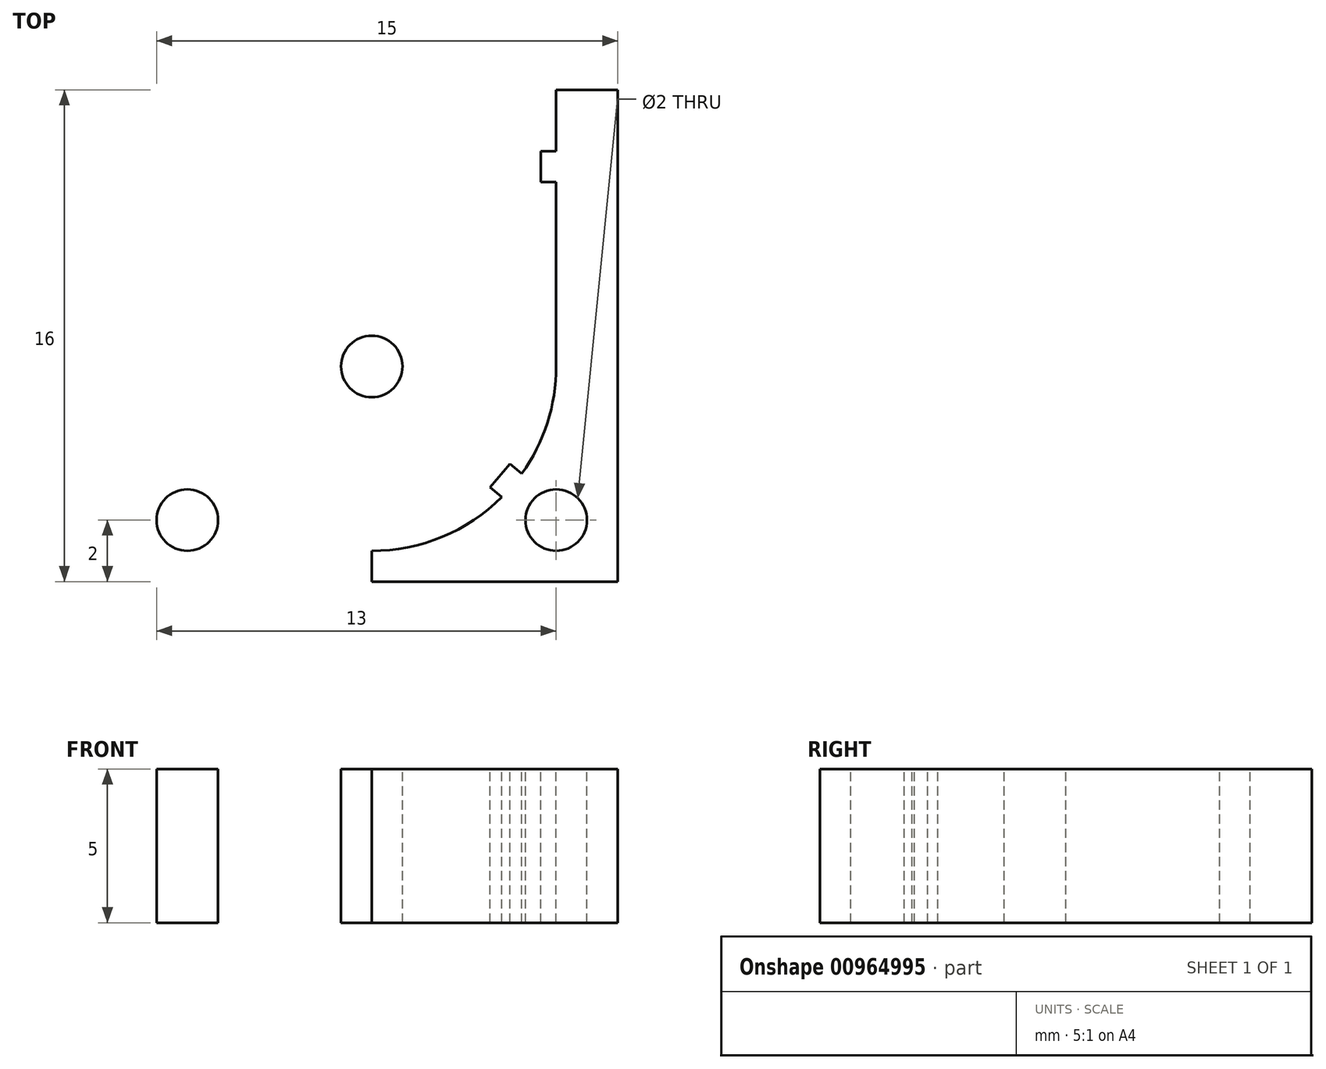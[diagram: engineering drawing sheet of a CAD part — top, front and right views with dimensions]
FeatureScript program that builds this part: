
annotation { "Feature Type Name" : "Feature", "Feature Type Description" : "" }
export const myFeature = defineFeature(function(context is Context, id is Id, definition is map)
    precondition{}
    {
        {
            var Q0;
            Q0=qCreatedBy(makeId("Top.planeOp"),FACE);
            var sketch = newSketch(context, id + "F0", { "sketchPlane" : qUnion([Q0])});
            skLineSegment(sketch, "E0.bottom", {"start": v(0, 0) * mm, "end": v(-16, 0) * mm});
            skLineSegment(sketch, "E0.top", {"start": v(0, 16) * mm, "end": v(-16, 16) * mm});
            skLineSegment(sketch, "E0.left", {"start": v(0, 0) * mm, "end": v(0, 16) * mm});
            skLineSegment(sketch, "E0.right", {"start": v(-16, 0) * mm, "end": v(-16, 16) * mm});
            skSolve(sketch);
        }
        {
            var Q0;
            Q0=makeQuery(id+"F0.imprint","IMPRINT",FACE,{"disambiguationData":[TD([[makeQuery(id+"F0.imprint","IMPRINT",EDGE,{"derivedFrom":sQuery(id+"F0.wireOp",EDGE,"E0.bottom")}),-1.0]])]});
            extrude(context, id + "F1", {"entities" : qUnion([Q0]), "depth" : 5 * mm, "offsetDistance" : 25 * mm});
        }
        {
            var Q0;
            Q0=makeQuery(id+"F1.opExtrude","CAP_FACE",FACE,{"disambiguationData":[OSD([sQuery(id+"F0.wireOp",EDGE,"E0.bottom"),sQuery(id+"F0.wireOp",EDGE,"E0.top"),sQuery(id+"F0.wireOp",EDGE,"E0.left"),sQuery(id+"F0.wireOp",EDGE,"E0.right")])],"isStart":false});
            var sketch = newSketch(context, id + "F2", { "sketchPlane" : qUnion([Q0])});
            skLineSegment(sketch, "E1", {"start": v(-16, 16) * mm, "end": v(-14, 16) * mm});
            skLineSegment(sketch, "E2", {"start": v(-14, 16) * mm, "end": v(-2, 16) * mm});
            skLineSegment(sketch, "E3", {"start": v(-2, 16) * mm, "end": v(0, 16) * mm});
            skLineSegment(sketch, "E4.bottom", {"start": v(-14, 16) * mm, "end": v(-12, 16) * mm});
            skLineSegment(sketch, "E4.top", {"start": v(-14, 7) * mm, "end": v(-12, 7) * mm});
            skLineSegment(sketch, "E4.left", {"start": v(-14, 16) * mm, "end": v(-14, 7) * mm});
            skLineSegment(sketch, "E4.right", {"start": v(-12, 16) * mm, "end": v(-12, 7) * mm});
            skLineSegment(sketch, "E5.bottom", {"start": v(-2, 16) * mm, "end": v(-4, 16) * mm});
            skLineSegment(sketch, "E5.top", {"start": v(-2, 7) * mm, "end": v(-4, 7) * mm});
            skLineSegment(sketch, "E5.left", {"start": v(-2, 16) * mm, "end": v(-2, 7) * mm});
            skLineSegment(sketch, "E5.right", {"start": v(-4, 16) * mm, "end": v(-4, 7) * mm});
            skArc(sketch, "E6", {"start": v(-12, 7) * mm, "mid": v(-8, 3) * mm, "end": v(-4, 7) * mm});
            skArc(sketch, "E7", {"start": v(-14, 7) * mm, "mid": v(-8, 1) * mm, "end": v(-2, 7) * mm});
            skLineSegment(sketch, "E8.0", {"start": v(-6, 16) * mm, "end": v(-6, 7) * mm});
            skArc(sketch, "E8.1", {"start": v(-10, 7) * mm, "mid": v(-8, 5) * mm, "end": v(-6, 7) * mm});
            skLineSegment(sketch, "E8.2", {"start": v(-10, 16) * mm, "end": v(-10, 7) * mm});
            skLineSegment(sketch, "E9", {"start": v(-8, 16) * mm, "end": v(-8, 7) * mm});
            skSolve(sketch);
        }
        {
            var Q0;
            Q0=makeQuery(id+"F2.imprint","IMPRINT",FACE,{"disambiguationData":[TD([[makeQuery(id+"F2.imprint","IMPRINT",EDGE,{"derivedFrom":sQuery(id+"F2.wireOp",EDGE,"E4.top")}),1.0]])]});
            var Q1;
            Q1=makeQuery(id+"F2.imprint","IMPRINT",FACE,{"disambiguationData":[TD([[makeQuery(id+"F2.imprint","IMPRINT",EDGE,{"derivedFrom":sQuery(id+"F2.wireOp",EDGE,"E4.top")}),-1.0]])]});
            var Q2;
            {var subQ3=sQuery(id+"F2.wireOp",EDGE,"E4.right");Q2=makeQuery(id+"F2.imprint","IMPRINT",FACE,{"disambiguationData":[TD([[makeQuery(id+"F2.imprint","IMPRINT",EDGE,{"derivedFrom":subQ3}),1.0]])]});}
            var Q3;
            Q3=makeQuery(id+"F2.imprint","IMPRINT",FACE,{"disambiguationData":[TD([[makeQuery(id+"F2.imprint","IMPRINT",EDGE,{"derivedFrom":sQuery(id+"F2.wireOp",EDGE,"E5.top")}),-1.0]])]});
            var Q4;
            Q4=makeQuery(id+"F2.imprint","IMPRINT",FACE,{"disambiguationData":[TD([[makeQuery(id+"F2.imprint","IMPRINT",EDGE,{"derivedFrom":sQuery(id+"F2.wireOp",EDGE,"E4.top")}),1.0]])]});
            var Q5;
            {var subQ4=sQuery(id+"F2.wireOp",EDGE,"v4n3mYmn-XXXl-4wGk-IPKp-ZQGeS8t006bx.top");Q5=makeQuery(id+"F2.imprint","IMPRINT",FACE,{"disambiguationData":[TD([[makeQuery(id+"F2.imprint","IMPRINT",EDGE,{"derivedFrom":subQ4}),-1.0]])]});}
            extrude(context, id + "F3", {"entities" : qUnion([Q0, Q1, Q2, Q3, Q4, Q5]), "operationType" : NewBodyOperationType.REMOVE, "oppositeDirection" : true, "depth" : 1.5 * mm, "offsetDistance" : 25 * mm});
        }
        {
            var Q0;
            Q0=makeQuery(id+"F3.boolean.opBoolean","COPY",FACE,{"derivedFrom":makeQuery(id+"F3.opExtrude","CAP_FACE",FACE,{"disambiguationData":[OSD([sQuery(id+"F2.wireOp",EDGE,"E2"),sQuery(id+"F2.wireOp",EDGE,"E4.left"),sQuery(id+"F2.wireOp",EDGE,"E5.left"),sQuery(id+"F2.wireOp",EDGE,"E7"),sQuery(id+"F2.wireOp",EDGE,"E8.0"),sQuery(id+"F2.wireOp",EDGE,"E8.1"),sQuery(id+"F2.wireOp",EDGE,"E8.2")])],"isStart":false})});
            var sketch = newSketch(context, id + "F4", { "sketchPlane" : qUnion([Q0])});
            skLineSegment(sketch, "E10", {"start": v(-16, 16) * mm, "end": v(-14, 16) * mm});
            skLineSegment(sketch, "E11", {"start": v(-14, 16) * mm, "end": v(-2, 16) * mm});
            skLineSegment(sketch, "E12", {"start": v(-2, 16) * mm, "end": v(0, 16) * mm});
            skLineSegment(sketch, "E13.bottom", {"start": v(-14, 16) * mm, "end": v(-12, 16) * mm});
            skLineSegment(sketch, "E13.top", {"start": v(-14, 7) * mm, "end": v(-12, 7) * mm});
            skLineSegment(sketch, "E13.left", {"start": v(-14, 16) * mm, "end": v(-14, 7) * mm});
            skLineSegment(sketch, "E13.right", {"start": v(-12, 16) * mm, "end": v(-12, 7) * mm});
            skLineSegment(sketch, "E14.bottom", {"start": v(-2, 16) * mm, "end": v(-4, 16) * mm});
            skLineSegment(sketch, "E14.top", {"start": v(-2, 7) * mm, "end": v(-4, 7) * mm});
            skLineSegment(sketch, "E14.left", {"start": v(-2, 16) * mm, "end": v(-2, 7) * mm});
            skLineSegment(sketch, "E14.right", {"start": v(-4, 16) * mm, "end": v(-4, 7) * mm});
            skArc(sketch, "E15", {"start": v(-12, 7) * mm, "mid": v(-8, 3) * mm, "end": v(-4, 7) * mm});
            skArc(sketch, "E16", {"start": v(-14, 7) * mm, "mid": v(-8, 1) * mm, "end": v(-2, 7) * mm});
            skLineSegment(sketch, "E17.0", {"start": v(-6, 16) * mm, "end": v(-6, 7) * mm});
            skArc(sketch, "E17.1", {"start": v(-10, 7) * mm, "mid": v(-8, 5) * mm, "end": v(-6, 7) * mm});
            skLineSegment(sketch, "E17.2", {"start": v(-10, 16) * mm, "end": v(-10, 7) * mm});
            skSolve(sketch);
        }
        {
            var Q0;
            Q0=makeQuery(id+"F4.imprint","IMPRINT",FACE,{"disambiguationData":[TD([[makeQuery(id+"F4.imprint","IMPRINT",EDGE,{"derivedFrom":sQuery(id+"F4.wireOp",EDGE,"E13.top")}),1.0]])]});
            var Q1;
            Q1=sQuery(id+"F4.wireOp",EDGE,"E13.right");
            revolve(context, id + "F5", {"operationType" : NewBodyOperationType.REMOVE, "surfaceOperationType" : NewSurfaceOperationType.NEW, "entities" : qUnion([Q0]), "axis" : qUnion([Q1]), "revolveType" : RevolveType.FULL, "oppositeDirection" : true});
        }
        {
            var Q0;
            Q0=makeQuery(id+"F5.boolean.opBoolean","COPY",FACE,{"derivedFrom":makeQuery(id+"F5.opRevolve","SWEPT_FACE",FACE,{"disambiguationData":[OSD([sQuery(id+"F4.wireOp",EDGE,"E13.top")])]})});
            var Q1;
            Q1=makeQuery(id+"F3.boolean.opBoolean","COPY",EDGE,{"derivedFrom":makeQuery(id+"F3.opExtrude","CAP_EDGE",EDGE,{"disambiguationData":[OSD([sQuery(id+"F2.wireOp",EDGE,"E8.1")])],"isStart":false})});
            sweep(context, id + "F6", {"operationType" : NewBodyOperationType.REMOVE, "profiles" : qUnion([Q0]), "path" : qUnion([Q1])});
        }
        {
            var Q0;
            Q0=makeQuery(id+"F4.imprint","IMPRINT",FACE,{"disambiguationData":[TD([[makeQuery(id+"F4.imprint","IMPRINT",EDGE,{"derivedFrom":sQuery(id+"F4.wireOp",EDGE,"E14.top")}),-1.0]])]});
            var Q1;
            Q1=sQuery(id+"F4.wireOp",EDGE,"E14.right");
            revolve(context, id + "F7", {"operationType" : NewBodyOperationType.REMOVE, "surfaceOperationType" : NewSurfaceOperationType.NEW, "entities" : qUnion([Q0]), "axis" : qUnion([Q1]), "revolveType" : RevolveType.FULL, "oppositeDirection" : true});
        }
        {
            var Q0;
            {var subQ0=sQuery(id+"F0.wireOp",EDGE,"E0.left");var subQ1=sQuery(id+"F0.wireOp",EDGE,"E0.top");var subQ2=sQuery(id+"F0.wireOp",EDGE,"E0.right");var subQ3=sQuery(id+"F0.wireOp",EDGE,"E0.bottom");Q0=makeQuery(id+"F3.boolean.opBoolean","SPLIT",FACE,{"disambiguationData":[TD([makeQuery(id+"F1.opExtrude","SWEPT_FACE",FACE,{"disambiguationData":[OSD([subQ3])]})])],"derivedFrom":makeQuery(id+"F1.opExtrude","CAP_FACE",FACE,{"disambiguationData":[OSD([subQ3,subQ1,subQ0,subQ2])],"isStart":false})});}
            var sketch = newSketch(context, id + "F8", { "sketchPlane" : qUnion([Q0])});
            skLineSegment(sketch, "E18", {"start": v(-16, 16) * mm, "end": v(0, 16) * mm});
            skLineSegment(sketch, "E19", {"start": v(-8, 16) * mm, "end": v(-8, 7) * mm});
            skLineSegment(sketch, "E20", {"start": v(-14, 16) * mm, "end": v(-14, 14) * mm});
            skLineSegment(sketch, "E21", {"start": v(-14, 14) * mm, "end": v(-13.5, 14) * mm});
            skLineSegment(sketch, "E22", {"start": v(-13.5, 14) * mm, "end": v(-13.5, 13) * mm});
            skLineSegment(sketch, "E23", {"start": v(-13.5, 13) * mm, "end": v(-14, 13) * mm});
            skLineSegment(sketch, "E24", {"start": v(-14, 13) * mm, "end": v(-14, 14) * mm});
            skLineSegment(sketch, "E25", {"start": v(-8, 7) * mm, "end": v(-14, 7) * mm});
            skLineSegment(sketch, "E26", {"start": v(-10, 7) * mm, "end": v(-10, 9) * mm});
            skLineSegment(sketch, "E27.bottom", {"start": v(-10, 9) * mm, "end": v(-10.5, 9) * mm});
            skLineSegment(sketch, "E27.top", {"start": v(-10, 10) * mm, "end": v(-10.5, 10) * mm});
            skLineSegment(sketch, "E27.left", {"start": v(-10, 9) * mm, "end": v(-10, 10) * mm});
            skLineSegment(sketch, "E27.right", {"start": v(-10.5, 9) * mm, "end": v(-10.5, 10) * mm});
            skLineSegment(sketch, "E28.MirrorCS", {"start": v(-6, 10) * mm, "end": v(-5.5, 10) * mm});
            skLineSegment(sketch, "E29.MirrorCS", {"start": v(-5.5, 9) * mm, "end": v(-5.5, 10) * mm});
            skLineSegment(sketch, "E30.MirrorCS", {"start": v(-6, 9) * mm, "end": v(-5.5, 9) * mm});
            skLineSegment(sketch, "E31.MirrorCS", {"start": v(-6, 9) * mm, "end": v(-6, 10) * mm});
            skLineSegment(sketch, "E32.MirrorCS", {"start": v(-2.5, 14) * mm, "end": v(-2.5, 13) * mm});
            skLineSegment(sketch, "E33.MirrorCS", {"start": v(-2, 14) * mm, "end": v(-2.5, 14) * mm});
            skLineSegment(sketch, "E34.MirrorCS", {"start": v(-2, 13) * mm, "end": v(-2, 14) * mm});
            skLineSegment(sketch, "E35.MirrorCS", {"start": v(-2.5, 13) * mm, "end": v(-2, 13) * mm});
            skLineSegment(sketch, "E36", {"start": v(-12.88, 3.5) * mm, "end": v(-12.5, 3.83) * mm});
            skLineSegment(sketch, "E37", {"start": v(-12.5, 3.83) * mm, "end": v(-11.85, 3.07) * mm});
            skLineSegment(sketch, "E38", {"start": v(-11.85, 3.07) * mm, "end": v(-12.23, 2.75) * mm});
            skLineSegment(sketch, "E39", {"start": v(-12.23, 2.75) * mm, "end": v(-12.88, 2.85) * mm});
            skLineSegment(sketch, "E40", {"start": v(-12.88, 2.85) * mm, "end": v(-12.88, 3.5) * mm});
            skLineSegment(sketch, "E41.MirrorCS", {"start": v(-3.5, 3.83) * mm, "end": v(-4.15, 3.07) * mm});
            skLineSegment(sketch, "E42.MirrorCS", {"start": v(-3.12, 3.5) * mm, "end": v(-3.5, 3.83) * mm});
            skLineSegment(sketch, "E43.MirrorCS", {"start": v(-4.15, 3.07) * mm, "end": v(-3.77, 2.75) * mm});
            skLineSegment(sketch, "E44", {"start": v(-8, 7) * mm, "end": v(-8, 1) * mm});
            skLineSegment(sketch, "E45", {"start": v(-8, 5) * mm, "end": v(-8.5, 5) * mm});
            skLineSegment(sketch, "E46", {"start": v(-8.5, 5) * mm, "end": v(-8.5, 4.5) * mm});
            skLineSegment(sketch, "E47", {"start": v(-8.5, 4.5) * mm, "end": v(-8, 4.5) * mm});
            skLineSegment(sketch, "E48", {"start": v(-8, 4.5) * mm, "end": v(-7.5, 4.5) * mm});
            skLineSegment(sketch, "E49", {"start": v(-7.5, 4.5) * mm, "end": v(-7.5, 5) * mm});
            skLineSegment(sketch, "E50", {"start": v(-7.5, 5) * mm, "end": v(-8, 5) * mm});
            skLineSegment(sketch, "E51.bottom", {"start": v(-7.5, 5) * mm, "end": v(-8.5, 5) * mm});
            skLineSegment(sketch, "E51.top", {"start": v(-7.5, 5.5) * mm, "end": v(-8.5, 5.5) * mm});
            skLineSegment(sketch, "E51.left", {"start": v(-7.5, 5) * mm, "end": v(-7.5, 5.5) * mm});
            skLineSegment(sketch, "E51.right", {"start": v(-8.5, 5) * mm, "end": v(-8.5, 5.5) * mm});
            skSolve(sketch);
        }
        {
            var Q0;
            Q0=makeQuery(id+"F8.imprint","IMPRINT",FACE,{"disambiguationData":[TD([[makeQuery(id+"F8.imprint","IMPRINT",EDGE,{"derivedFrom":sQuery(id+"F8.wireOp",EDGE,"E21")}),-1.0]])]});
            var Q1;
            Q1=makeQuery(id+"F8.imprint","IMPRINT",FACE,{"disambiguationData":[TD([[makeQuery(id+"F8.imprint","IMPRINT",EDGE,{"derivedFrom":sQuery(id+"F8.wireOp",EDGE,"E27.bottom")}),-1.0]])]});
            var Q2;
            Q2=makeQuery(id+"F8.imprint","IMPRINT",FACE,{"disambiguationData":[TD([[makeQuery(id+"F8.imprint","IMPRINT",EDGE,{"derivedFrom":sQuery(id+"F8.wireOp",EDGE,"E28.MirrorCS")}),-1.0]])]});
            var Q3;
            Q3=makeQuery(id+"F8.imprint","IMPRINT",FACE,{"disambiguationData":[TD([[makeQuery(id+"F8.imprint","IMPRINT",EDGE,{"derivedFrom":sQuery(id+"F8.wireOp",EDGE,"E32.MirrorCS")}),1.0]])]});
            var Q4;
            {var subQ0=sQuery(id+"F8.wireOp",EDGE,"E36");Q4=makeQuery(id+"F8.imprint","IMPRINT",FACE,{"disambiguationData":[TD([[makeQuery(id+"F8.imprint","IMPRINT",EDGE,{"derivedFrom":subQ0}),-1.0]])]});}
            var Q5;
            Q5=makeQuery(id+"F8.imprint","IMPRINT",FACE,{"disambiguationData":[TD([[makeQuery(id+"F8.imprint","IMPRINT",EDGE,{"derivedFrom":sQuery(id+"F8.wireOp",EDGE,"E41.MirrorCS")}),1.0]])]});
            var Q6;
            {var subQ2=sQuery(id+"F8.wireOp",EDGE,"E45");Q6=makeQuery(id+"F8.imprint","IMPRINT",FACE,{"disambiguationData":[TD([[makeQuery(id+"F8.imprint","IMPRINT",EDGE,{"derivedFrom":subQ2}),1.0]])]});}
            var Q7;
            {var subQ0=sQuery(id+"F8.wireOp",EDGE,"E48");Q7=makeQuery(id+"F8.imprint","IMPRINT",FACE,{"disambiguationData":[TD([[makeQuery(id+"F8.imprint","IMPRINT",EDGE,{"derivedFrom":subQ0}),1.0]])]});}
            var Q8;
            {var subQ0=sQuery(id+"F8.wireOp",EDGE,"E45");Q8=makeQuery(id+"F8.imprint","IMPRINT",FACE,{"disambiguationData":[TD([[makeQuery(id+"F8.imprint","IMPRINT",EDGE,{"derivedFrom":subQ0}),-1.0]])]});}
            var Q9;
            {var subQ0=sQuery(id+"F8.wireOp",EDGE,"E50");Q9=makeQuery(id+"F8.imprint","IMPRINT",FACE,{"disambiguationData":[TD([[makeQuery(id+"F8.imprint","IMPRINT",EDGE,{"derivedFrom":subQ0}),-1.0]])]});}
            extrude(context, id + "F9", {"entities" : qUnion([Q0, Q1, Q2, Q3, Q4, Q5, Q6, Q7, Q8, Q9]), "operationType" : NewBodyOperationType.ADD, "oppositeDirection" : true, "depth" : 5 * mm, "offsetDistance" : 25 * mm});
        }
        {
            var Q0;
            {var subQ0=sQuery(id+"F2.wireOp",EDGE,"E7");var subQ1=sQuery(id+"F0.wireOp",EDGE,"E0.left");var subQ2=sQuery(id+"F0.wireOp",EDGE,"E0.top");var subQ3=sQuery(id+"F0.wireOp",EDGE,"E0.right");var subQ4=sQuery(id+"F0.wireOp",EDGE,"E0.bottom");Q0=makeQuery(id+"F9.boolean.opBoolean","MERGE",FACE,{"derivedFrom":[makeQuery(id+"F3.boolean.opBoolean","SPLIT",FACE,{"disambiguationData":[TD([makeQuery(id+"F1.opExtrude","SWEPT_FACE",FACE,{"disambiguationData":[OSD([subQ4])]})])],"derivedFrom":makeQuery(id+"F1.opExtrude","CAP_FACE",FACE,{"disambiguationData":[OSD([subQ4,subQ2,subQ1,subQ3])],"isStart":false})}),makeQuery(id+"F9.opExtrude","CAP_FACE",FACE,{"disambiguationData":[OSD([sQuery(id+"F8.wireOp",EDGE,"E21"),sQuery(id+"F8.wireOp",EDGE,"E22"),sQuery(id+"F8.wireOp",EDGE,"E23"),sQuery(id+"F8.wireOp",EDGE,"E24")])],"isStart":true}),makeQuery(id+"F9.opExtrude","CAP_FACE",FACE,{"disambiguationData":[OSD([sQuery(id+"F8.wireOp",EDGE,"E32.MirrorCS"),sQuery(id+"F8.wireOp",EDGE,"E33.MirrorCS"),sQuery(id+"F8.wireOp",EDGE,"E34.MirrorCS"),sQuery(id+"F8.wireOp",EDGE,"E35.MirrorCS")])],"isStart":true}),makeQuery(id+"F9.opExtrude","CAP_FACE",FACE,{"disambiguationData":[OSD([subQ0,sQuery(id+"F8.wireOp",EDGE,"E36"),sQuery(id+"F8.wireOp",EDGE,"E37"),sQuery(id+"F8.wireOp",EDGE,"E38")])],"isStart":true}),makeQuery(id+"F9.opExtrude","CAP_FACE",FACE,{"disambiguationData":[OSD([subQ0,sQuery(id+"F8.wireOp",EDGE,"E41.MirrorCS"),sQuery(id+"F8.wireOp",EDGE,"E42.MirrorCS"),sQuery(id+"F8.wireOp",EDGE,"E43.MirrorCS")])],"isStart":true})]});}
            var sketch = newSketch(context, id + "F10", { "sketchPlane" : qUnion([Q0])});
            skCircle(sketch, "E52", {"center": v(-2, 2) * mm, "radius": 1 * mm});
            skLineSegment(sketch, "E53", {"start": v(-16, 16) * mm, "end": v(0, 16) * mm});
            skLineSegment(sketch, "E54", {"start": v(-8, 0) * mm, "end": v(-8, 16) * mm});
            skCircle(sketch, "E55.MirrorC", {"center": v(-14, 2) * mm, "radius": 1 * mm});
            skCircle(sketch, "E56", {"center": v(-8, 7) * mm, "radius": 1 * mm});
            skCircle(sketch, "E57", {"center": v(-8, 14) * mm, "radius": 1 * mm});
            skSolve(sketch);
        }
        {
            var Q0;
            {var subQ0=sQuery(id+"F10.wireOp",EDGE,"E57");var subQ1=sQuery(id+"F10.wireOp",EDGE,"E54");var subQ2=makeQuery(id+"F10.imprint","INTERSECT",VERTEX,{"disambiguationData":[OD(0.0)],"derivedFrom":[subQ1,subQ0]});Q0=makeQuery(id+"F10.imprint","IMPRINT",FACE,{"disambiguationData":[TD([[makeQuery(id+"F10.imprint","IMPRINT",EDGE,{"disambiguationData":[TD([[subQ2,-1.0]])],"derivedFrom":subQ1}),-1.0]])]});}
            var Q1;
            {var subQ0=sQuery(id+"F10.wireOp",EDGE,"E57");var subQ1=sQuery(id+"F10.wireOp",EDGE,"E54");var subQ2=makeQuery(id+"F10.imprint","INTERSECT",VERTEX,{"disambiguationData":[OD(0.0)],"derivedFrom":[subQ1,subQ0]});Q1=makeQuery(id+"F10.imprint","IMPRINT",FACE,{"disambiguationData":[TD([[makeQuery(id+"F10.imprint","IMPRINT",EDGE,{"disambiguationData":[TD([[subQ2,-1.0]])],"derivedFrom":subQ1}),1.0]])]});}
            var Q2;
            {var subQ0=sQuery(id+"F10.wireOp",EDGE,"E56");var subQ1=sQuery(id+"F10.wireOp",EDGE,"E54");var subQ2=makeQuery(id+"F10.imprint","INTERSECT",VERTEX,{"disambiguationData":[OD(0.0)],"derivedFrom":[subQ1,subQ0]});Q2=makeQuery(id+"F10.imprint","IMPRINT",FACE,{"disambiguationData":[TD([[makeQuery(id+"F10.imprint","IMPRINT",EDGE,{"disambiguationData":[TD([[subQ2,-1.0]])],"derivedFrom":subQ1}),-1.0]])]});}
            var Q3;
            {var subQ0=sQuery(id+"F10.wireOp",EDGE,"E56");var subQ1=sQuery(id+"F10.wireOp",EDGE,"E54");var subQ2=makeQuery(id+"F10.imprint","INTERSECT",VERTEX,{"disambiguationData":[OD(0.0)],"derivedFrom":[subQ1,subQ0]});Q3=makeQuery(id+"F10.imprint","IMPRINT",FACE,{"disambiguationData":[TD([[makeQuery(id+"F10.imprint","IMPRINT",EDGE,{"disambiguationData":[TD([[subQ2,-1.0]])],"derivedFrom":subQ1}),1.0]])]});}
            var Q4;
            Q4=makeQuery(id+"F10.imprint","IMPRINT",FACE,{"disambiguationData":[TD([[makeQuery(id+"F10.imprint","IMPRINT",EDGE,{"derivedFrom":sQuery(id+"F10.wireOp",EDGE,"E55.MirrorC")}),-1.0]])]});
            var Q5;
            Q5=makeQuery(id+"F10.imprint","IMPRINT",FACE,{"disambiguationData":[TD([[makeQuery(id+"F10.imprint","IMPRINT",EDGE,{"derivedFrom":sQuery(id+"F10.wireOp",EDGE,"E52")}),1.0]])]});
            extrude(context, id + "F11", {"entities" : qUnion([Q0, Q1, Q2, Q3, Q4, Q5]), "operationType" : NewBodyOperationType.REMOVE, "oppositeDirection" : true, "depth" : 25 * mm, "offsetDistance" : 25 * mm});
        }
    });
